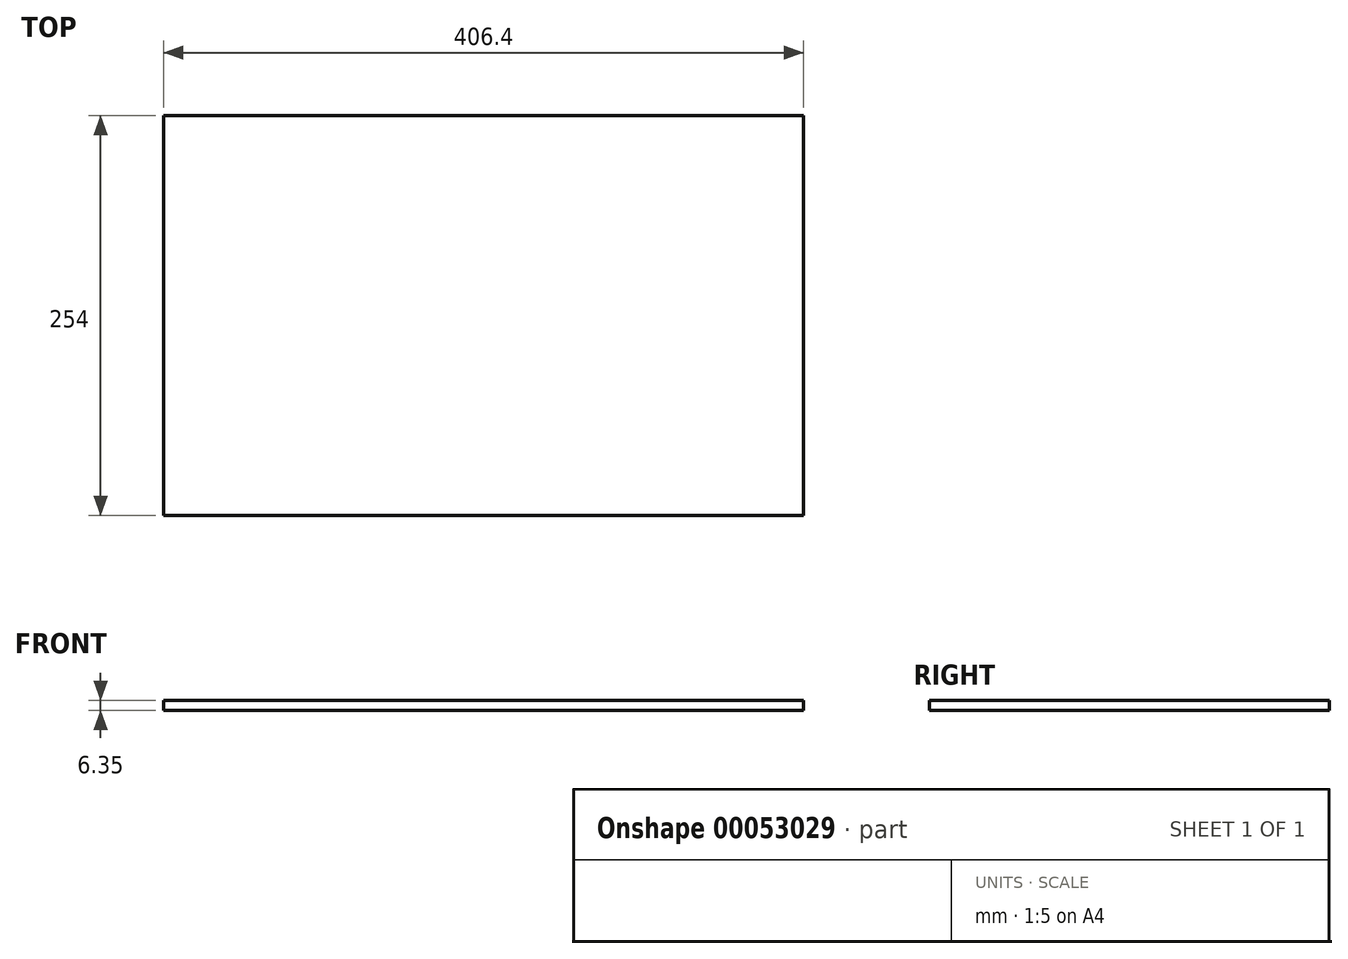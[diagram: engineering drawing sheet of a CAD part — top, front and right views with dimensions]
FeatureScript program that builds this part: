
annotation { "Feature Type Name" : "Feature", "Feature Type Description" : "" }
export const myFeature = defineFeature(function(context is Context, id is Id, definition is map)
    precondition{}
    {
        {
            var Q0;
            Q0=qCreatedBy(makeId("Top.planeOp"),FACE);
            var sketch = newSketch(context, id + "F0", { "sketchPlane" : qUnion([Q0])});
            skLineSegment(sketch, "E0.bottom", {"start": v(0, 0) * mm, "end": v(-406.4, 0) * mm});
            skLineSegment(sketch, "E0.top", {"start": v(0, -254) * mm, "end": v(-406.4, -254) * mm});
            skLineSegment(sketch, "E0.left", {"start": v(0, 0) * mm, "end": v(0, -254) * mm});
            skLineSegment(sketch, "E0.right", {"start": v(-406.4, 0) * mm, "end": v(-406.4, -254) * mm});
            skSolve(sketch);
        }
        {
            var Q0;
            Q0 = qSketchRegion(id + "F0", true);
            extrude(context, id + "F1", {"entities" : qUnion([Q0]), "depth" : 6.35 * mm});
        }
    });
